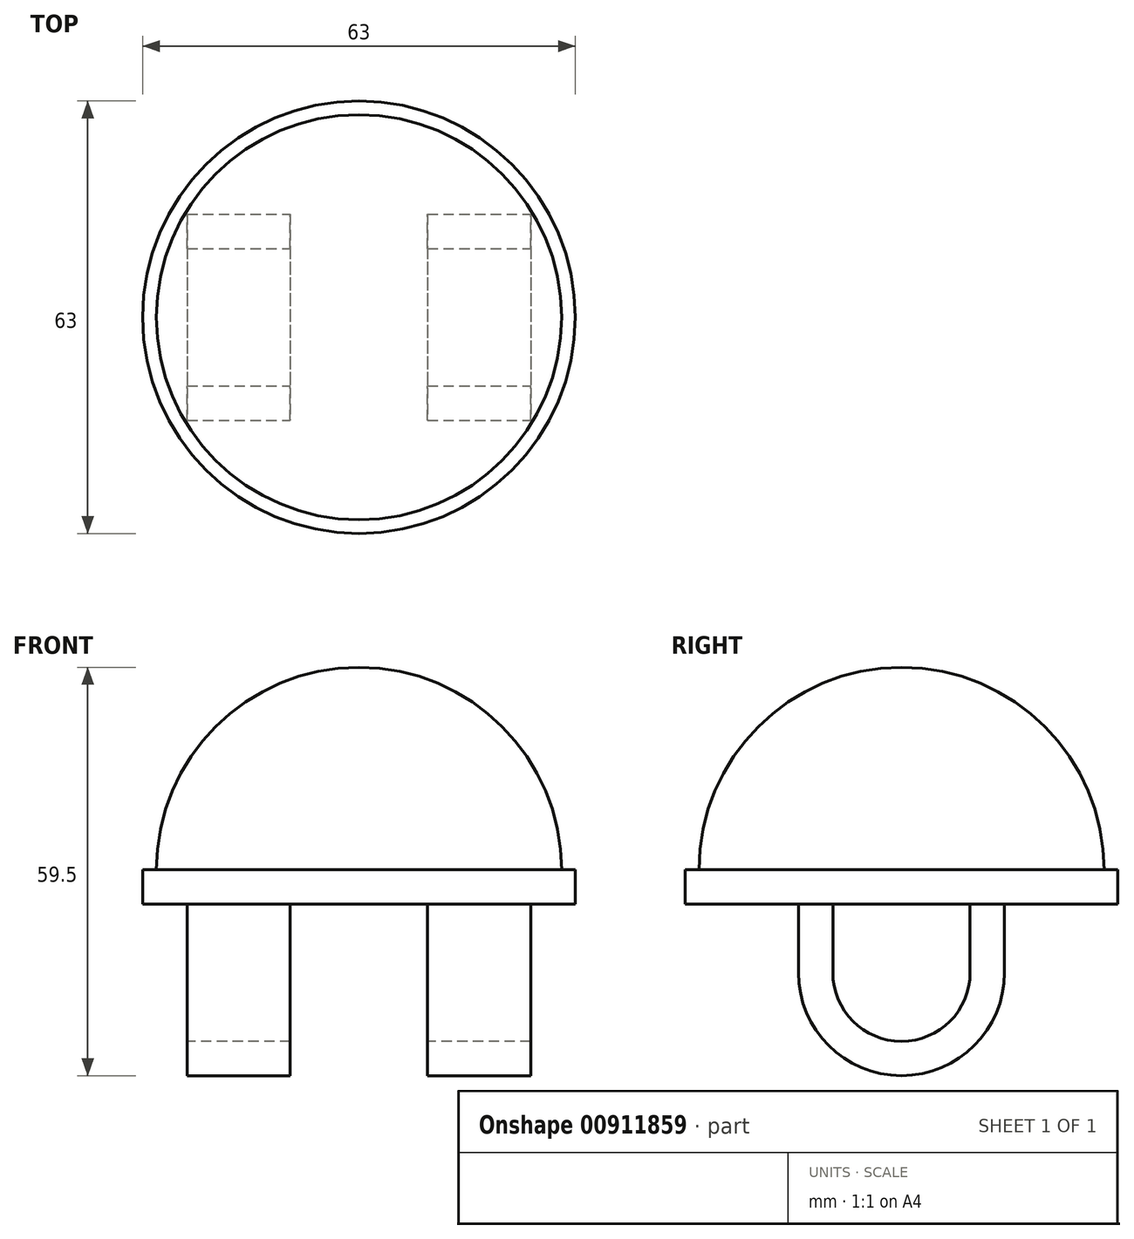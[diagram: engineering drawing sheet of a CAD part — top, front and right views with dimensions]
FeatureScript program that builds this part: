
annotation { "Feature Type Name" : "Feature", "Feature Type Description" : "" }
export const myFeature = defineFeature(function(context is Context, id is Id, definition is map)
    precondition{}
    {
        {
            var Q0;
            Q0=qCreatedBy(makeId("Top.planeOp"),FACE);
            var sketch = newSketch(context, id + "F0", { "sketchPlane" : qUnion([Q0])});
            skCircle(sketch, "E0", {"center": v(0, 0) * mm, "radius": 29.5 * mm});
            skLineSegment(sketch, "E1", {"start": v(0, 29.5) * mm, "end": v(0, -29.5) * mm});
            skSolve(sketch);
        }
        {
            var Q0;
            {var subQ0=sQuery(id+"F0.wireOp",EDGE,"E1");Q0=makeQuery(id+"F0.imprint","IMPRINT",FACE,{"disambiguationData":[TD([[makeQuery(id+"F0.imprint","IMPRINT",EDGE,{"derivedFrom":subQ0}),1.0]])]});}
            var Q1;
            Q1=sQuery(id+"F0.wireOp",EDGE,"E1");
            revolve(context, id + "F1", {"surfaceOperationType" : NewSurfaceOperationType.NEW, "entities" : qUnion([Q0]), "axis" : qUnion([Q1]), "revolveType" : RevolveType.ONE_DIRECTION, "angle" : 180 * degree});
        }
        {
            var Q0;
            Q0=makeQuery(id+"F1.opRevolve","CAP_FACE",FACE,{"disambiguationData":[OSD([sQuery(id+"F0.wireOp",EDGE,"E0"),sQuery(id+"F0.wireOp",EDGE,"E1")])],"isStart":true});
            var sketch = newSketch(context, id + "F2", { "sketchPlane" : qUnion([Q0])});
            skCircle(sketch, "E2", {"center": v(0, 0) * mm, "radius": 31.5 * mm});
            skSolve(sketch);
        }
        {
            var Q0;
            Q0=qSketchRegion(id+"F2",true);
            extrude(context, id + "F3", {"entities" : qUnion([Q0]), "operationType" : NewBodyOperationType.ADD, "depth" : 5 * mm, "offsetDistance" : 25 * mm});
        }
        {
            var Q0;
            Q0=makeQuery(id+"F3.opExtrude","CAP_FACE",FACE,{"disambiguationData":[OSD([sQuery(id+"F2.wireOp",EDGE,"E2")])],"isStart":false});
            var sketch = newSketch(context, id + "F4", { "sketchPlane" : qUnion([Q0])});
            skLineSegment(sketch, "E3.bottom", {"start": v(-25, 15) * mm, "end": v(-10, 15) * mm});
            skLineSegment(sketch, "E3.top", {"start": v(-25, 10) * mm, "end": v(-10, 10) * mm});
            skLineSegment(sketch, "E3.left", {"start": v(-25, 15) * mm, "end": v(-25, 10) * mm});
            skLineSegment(sketch, "E3.right", {"start": v(-10, 15) * mm, "end": v(-10, 10) * mm});
            skLineSegment(sketch, "E4.bottom", {"start": v(-25, -10) * mm, "end": v(-10, -10) * mm});
            skLineSegment(sketch, "E4.top", {"start": v(-25, -15) * mm, "end": v(-10, -15) * mm});
            skLineSegment(sketch, "E4.left", {"start": v(-25, -10) * mm, "end": v(-25, -15) * mm});
            skLineSegment(sketch, "E4.right", {"start": v(-10, -10) * mm, "end": v(-10, -15) * mm});
            skLineSegment(sketch, "E5.bottom", {"start": v(10, 15) * mm, "end": v(25, 15) * mm});
            skLineSegment(sketch, "E5.top", {"start": v(10, 10) * mm, "end": v(25, 10) * mm});
            skLineSegment(sketch, "E5.left", {"start": v(10, 15) * mm, "end": v(10, 10) * mm});
            skLineSegment(sketch, "E5.right", {"start": v(25, 15) * mm, "end": v(25, 10) * mm});
            skLineSegment(sketch, "E6.bottom", {"start": v(10, -10) * mm, "end": v(25, -10) * mm});
            skLineSegment(sketch, "E6.top", {"start": v(10, -15) * mm, "end": v(25, -15) * mm});
            skLineSegment(sketch, "E6.left", {"start": v(10, -10) * mm, "end": v(10, -15) * mm});
            skLineSegment(sketch, "E6.right", {"start": v(25, -10) * mm, "end": v(25, -15) * mm});
            skSolve(sketch);
        }
        {
            var Q0;
            Q0=makeQuery(id+"F4.imprint","IMPRINT",FACE,{"disambiguationData":[TD([[makeQuery(id+"F4.imprint","IMPRINT",EDGE,{"derivedFrom":sQuery(id+"F4.wireOp",EDGE,"E3.bottom")}),-1.0]])]});
            var Q1;
            Q1=makeQuery(id+"F4.imprint","IMPRINT",FACE,{"disambiguationData":[TD([[makeQuery(id+"F4.imprint","IMPRINT",EDGE,{"derivedFrom":sQuery(id+"F4.wireOp",EDGE,"E4.bottom")}),-1.0]])]});
            var Q2;
            Q2=makeQuery(id+"F4.imprint","IMPRINT",FACE,{"disambiguationData":[TD([[makeQuery(id+"F4.imprint","IMPRINT",EDGE,{"derivedFrom":sQuery(id+"F4.wireOp",EDGE,"E5.bottom")}),-1.0]])]});
            var Q3;
            Q3=makeQuery(id+"F4.imprint","IMPRINT",FACE,{"disambiguationData":[TD([[makeQuery(id+"F4.imprint","IMPRINT",EDGE,{"derivedFrom":sQuery(id+"F4.wireOp",EDGE,"E6.bottom")}),-1.0]])]});
            extrude(context, id + "F5", {"entities" : qUnion([Q0, Q1, Q2, Q3]), "operationType" : NewBodyOperationType.ADD, "depth" : 10 * mm, "offsetDistance" : 25 * mm});
        }
        {
            var Q0;
            Q0=makeQuery(id+"F5.opExtrude","CAP_FACE",FACE,{"disambiguationData":[OSD([sQuery(id+"F4.wireOp",EDGE,"E3.bottom"),sQuery(id+"F4.wireOp",EDGE,"E3.top"),sQuery(id+"F4.wireOp",EDGE,"E3.left"),sQuery(id+"F4.wireOp",EDGE,"E3.right")])],"isStart":false});
            var sketch = newSketch(context, id + "F6", { "sketchPlane" : qUnion([Q0])});
            skLineSegment(sketch, "E7", {"start": v(-38.57, 0) * mm, "end": v(41.22, 0) * mm});
            skSolve(sketch);
        }
        {
            var Q0;
            Q0=qSketchRegion(id+"F6",true);
            var Q1;
            Q1=makeQuery(id+"F6.imprint","IMPRINT",FACE,{"disambiguationData":[TD([[makeQuery(id+"F6.imprint","IMPRINT",EDGE,{"derivedFrom":makeQuery(id+"F5.opExtrude","CAP_EDGE",EDGE,{"disambiguationData":[OSD([sQuery(id+"F4.wireOp",EDGE,"E3.bottom")])],"isStart":false})}),-1.0]])]});
            var Q2;
            Q2=makeQuery(id+"F5.opExtrude","CAP_FACE",FACE,{"disambiguationData":[OSD([sQuery(id+"F4.wireOp",EDGE,"E5.bottom"),sQuery(id+"F4.wireOp",EDGE,"E5.top"),sQuery(id+"F4.wireOp",EDGE,"E5.left"),sQuery(id+"F4.wireOp",EDGE,"E5.right")])],"isStart":false});
            var Q3;
            Q3=sQuery(id+"F6.wireOp",EDGE,"E7");
            revolve(context, id + "F7", {"operationType" : NewBodyOperationType.ADD, "surfaceOperationType" : NewSurfaceOperationType.NEW, "entities" : qUnion([Q0, Q1, Q2]), "axis" : qUnion([Q3]), "revolveType" : RevolveType.ONE_DIRECTION, "angle" : 180 * degree});
        }
    });
